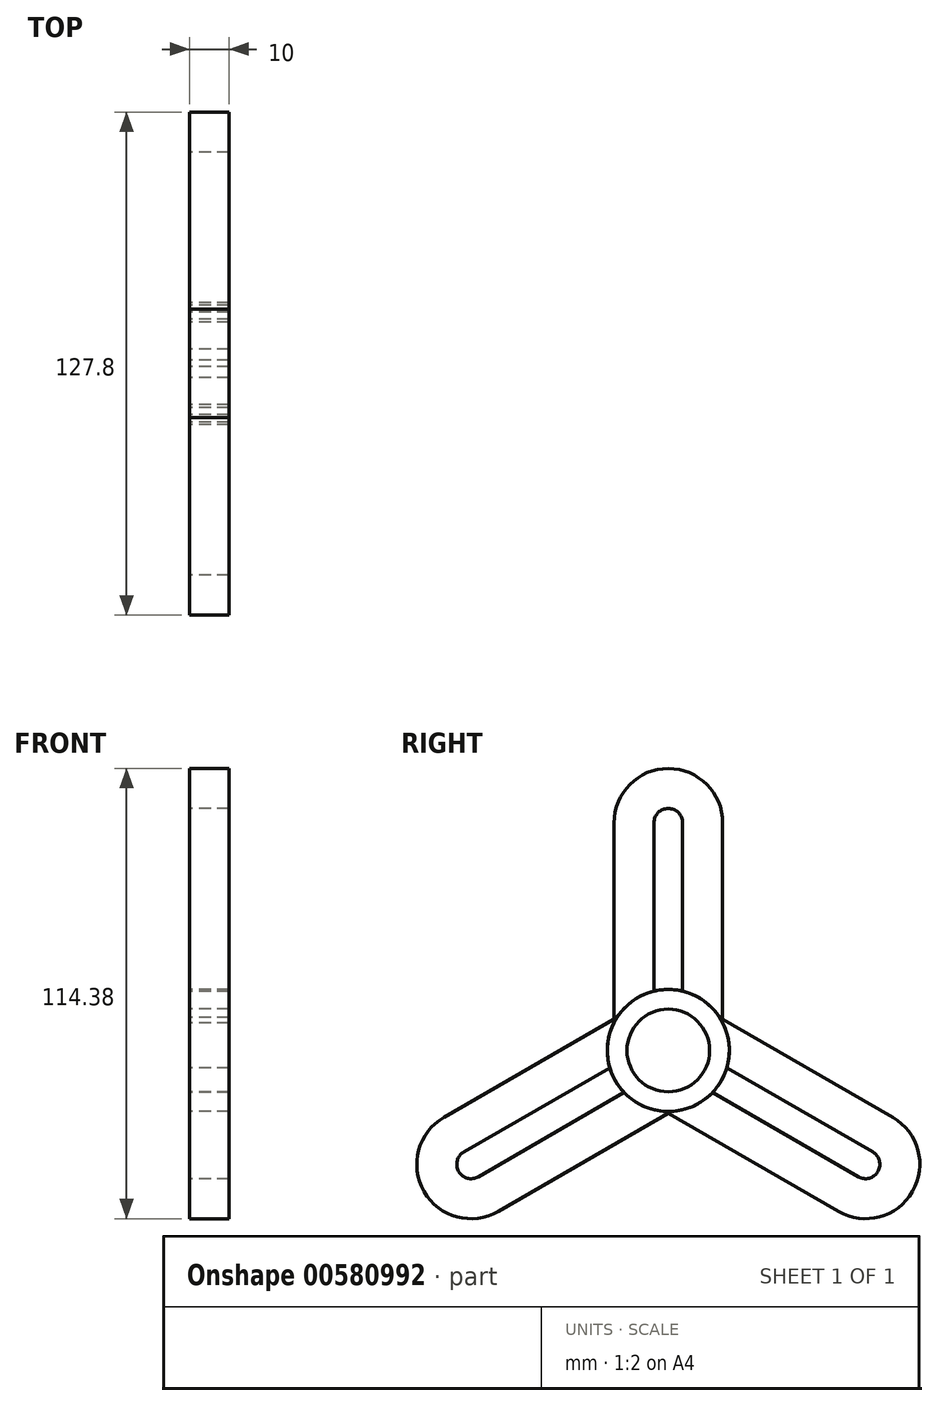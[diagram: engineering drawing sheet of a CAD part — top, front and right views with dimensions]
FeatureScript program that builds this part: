
annotation { "Feature Type Name" : "Feature", "Feature Type Description" : "" }
export const myFeature = defineFeature(function(context is Context, id is Id, definition is map)
    precondition{}
    {
        {
            var Q0;
            Q0=qCreatedBy(makeId("Right.planeOp"),FACE);
            var sketch = newSketch(context, id + "F0", { "sketchPlane" : qUnion([Q0])});
            skCircle(sketch, "E0", {"center": v(0, 0) * mm, "radius": 10.5 * mm});
            skCircle(sketch, "E1", {"center": v(0, 0) * mm, "radius": 15.5 * mm});
            skLineSegment(sketch, "E2", {"start": v(-3.65, 57.85) * mm, "end": v(-3.65, 15.07) * mm});
            skLineSegment(sketch, "E3", {"start": v(3.65, 57.85) * mm, "end": v(3.65, 15.07) * mm});
            skLineSegment(sketch, "E4", {"start": v(-13.8, 57.85) * mm, "end": v(-13.8, 7.05) * mm});
            skLineSegment(sketch, "E5", {"start": v(13.8, 57.85) * mm, "end": v(13.8, 7.05) * mm});
            skArc(sketch, "E6", {"start": v(13.8, 57.85) * mm, "mid": v(0, 71.65) * mm, "end": v(-13.8, 57.85) * mm});
            skArc(sketch, "E7", {"start": v(3.65, 57.85) * mm, "mid": v(0, 61.5) * mm, "end": v(-3.65, 57.85) * mm});
            skSolve(sketch);
        }
        {
            var Q0;
            {var subQ0=sQuery(id+"F0.wireOp",EDGE,"E2");Q0=makeQuery(id+"F0.imprint","IMPRINT",FACE,{"disambiguationData":[TD([[makeQuery(id+"F0.imprint","IMPRINT",EDGE,{"derivedFrom":subQ0}),-1.0]])]});}
            var Q1;
            Q1=makeQuery(id+"F0.imprint","IMPRINT",FACE,{"disambiguationData":[TD([[makeQuery(id+"F0.imprint","IMPRINT",EDGE,{"derivedFrom":sQuery(id+"F0.wireOp",EDGE,"E0")}),-1.0]])]});
            extrude(context, id + "F1", {"entities" : qUnion([Q0, Q1]), "depth" : 10 * mm, "offsetDistance" : 25.4 * mm});
        }
        {
            var Q0;
            Q0=makeQuery(id+"F1.opExtrude","SWEPT_BODY",BODY,{"disambiguationData":[OSD([sQuery(id+"F0.wireOp",EDGE,"E0"),sQuery(id+"F0.wireOp",EDGE,"E1"),sQuery(id+"F0.wireOp",EDGE,"E2"),sQuery(id+"F0.wireOp",EDGE,"E3"),sQuery(id+"F0.wireOp",EDGE,"E4"),sQuery(id+"F0.wireOp",EDGE,"E5"),sQuery(id+"F0.wireOp",EDGE,"WxM8BBLI-TLiK-yYHa-aPRE-7Dn1KHeZpDfc"),sQuery(id+"F0.wireOp",EDGE,"gNI2E30r-I6v4-F2Fh-XbbP-6JywbwIZJmRQ")])]});
            var Q1;
            Q1=makeQuery(id+"F1.opExtrude","CAP_EDGE",EDGE,{"disambiguationData":[OSD([sQuery(id+"F0.wireOp",EDGE,"E0")])],"isStart":false});
            circularPattern(context, id + "F2", {"entities" : qUnion([Q0]), "axis" : qUnion([Q1]), "angle" : 360 * degree, "instanceCount" : 3, "equalSpace" : true});
        }
    });
